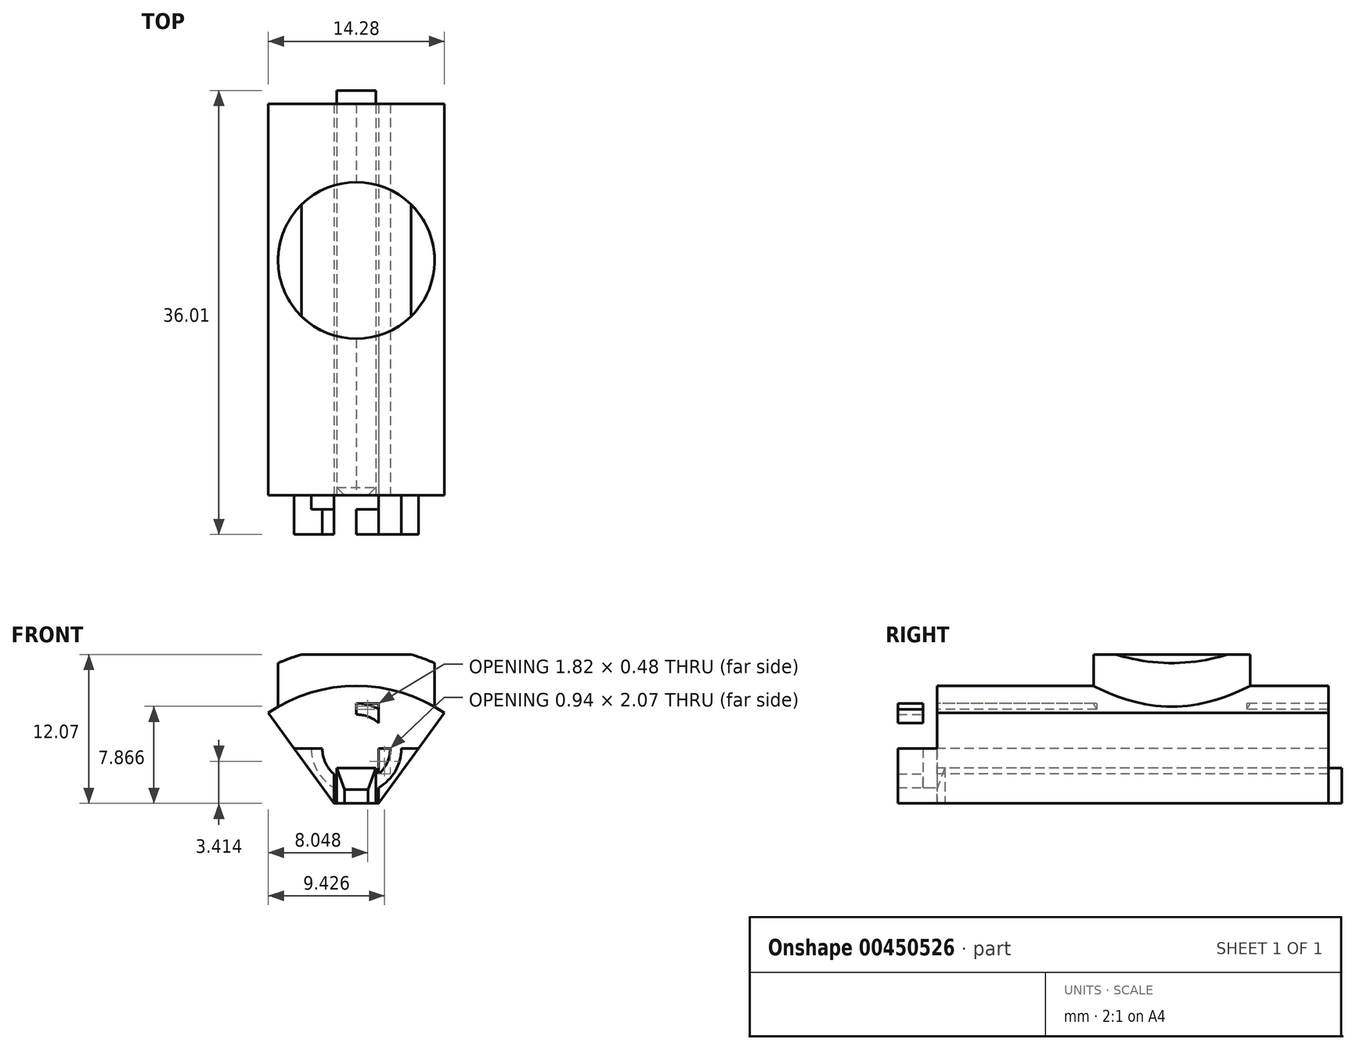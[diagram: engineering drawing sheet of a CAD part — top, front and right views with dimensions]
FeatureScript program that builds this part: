
annotation { "Feature Type Name" : "Feature", "Feature Type Description" : "" }
export const myFeature = defineFeature(function(context is Context, id is Id, definition is map)
    precondition{}
    {
        {
            var Q0;
            Q0=qCreatedBy(makeId("Front.planeOp"),FACE);
            var sketch = newSketch(context, id + "F0", { "sketchPlane" : qUnion([Q0])});
            skLineSegment(sketch, "E0", {"start": v(0, 0) * mm, "end": v(-7.46, 10.27) * mm});
            skLineSegment(sketch, "E1", {"start": v(0, 0) * mm, "end": v(7.46, 10.27) * mm});
            skArc(sketch, "E2", {"start": v(7.46, 10.27) * mm, "mid": v(0, 12.7) * mm, "end": v(-7.46, 10.27) * mm});
            skCircle(sketch, "E3", {"center": v(0, 7.62) * mm, "radius": 3.97 * mm});
            skCircle(sketch, "E4", {"center": v(0, 7.62) * mm, "radius": 3.66 * mm});
            skCircle(sketch, "E5", {"center": v(0, 7.62) * mm, "radius": 2.76 * mm});
            skLineSegment(sketch, "E6", {"start": v(3.41, 5.37) * mm, "end": v(7.14, 10.5) * mm});
            skLineSegment(sketch, "E7", {"start": v(3.41, 5.37) * mm, "end": v(0, 0.68) * mm});
            skLineSegment(sketch, "E8", {"start": v(-3.41, 5.37) * mm, "end": v(-7.14, 10.5) * mm});
            skLineSegment(sketch, "E9", {"start": v(-3.41, 5.37) * mm, "end": v(0, 0.68) * mm});
            skLineSegment(sketch, "E10", {"start": v(0, 11.28) * mm, "end": v(5.84, 11.28) * mm});
            skLineSegment(sketch, "E11", {"start": v(0, 11.28) * mm, "end": v(-5.84, 11.28) * mm});
            skPoint(sketch, "E12.orphan", {"position": v(0, 12.7) * mm});
            skArc(sketch, "E13", {"start": v(1.87, 2.57) * mm, "mid": v(0, 3.17) * mm, "end": v(-1.87, 2.57) * mm});
            skArc(sketch, "E14", {"start": v(-5.6, 7.7) * mm, "mid": v(-4.37, 9.58) * mm, "end": v(-4.68, 11.8) * mm});
            skArc(sketch, "E15", {"start": v(4.68, 11.8) * mm, "mid": v(4.37, 9.58) * mm, "end": v(5.6, 7.7) * mm});
            skLineSegment(sketch, "E16", {"start": v(0, 7.62) * mm, "end": v(-5.54, 7.62) * mm});
            skLineSegment(sketch, "E17", {"start": v(0, 7.62) * mm, "end": v(5.54, 7.62) * mm});
            skLineSegment(sketch, "E18", {"start": v(-1.82, 3.17) * mm, "end": v(-1.82, 12.57) * mm});
            skLineSegment(sketch, "E19", {"start": v(1.82, 3.17) * mm, "end": v(1.82, 12.57) * mm});
            skLineSegment(sketch, "E20", {"start": v(0, 6.03) * mm, "end": v(1.82, 6.03) * mm});
            skLineSegment(sketch, "E21", {"start": v(0, 6.03) * mm, "end": v(-1.82, 6.03) * mm});
            skLineSegment(sketch, "E22", {"start": v(0, 12.7) * mm, "end": v(0, 9.53) * mm});
            skLineSegment(sketch, "E23", {"start": v(0, 9.53) * mm, "end": v(-1.82, 9.53) * mm});
            skLineSegment(sketch, "E24", {"start": v(0, 9.53) * mm, "end": v(1.82, 9.53) * mm});
            skLineSegment(sketch, "E25", {"start": v(0, 0) * mm, "end": v(0, 6.03) * mm});
            skLineSegment(sketch, "E26", {"start": v(0, 3.17) * mm, "end": v(0.8, 3.17) * mm});
            skLineSegment(sketch, "E27", {"start": v(0, 3.17) * mm, "end": v(-0.8, 3.17) * mm});
            skLineSegment(sketch, "E28", {"start": v(0.8, 3.17) * mm, "end": v(1.82, 3.17) * mm});
            skLineSegment(sketch, "E29", {"start": v(-0.8, 3.17) * mm, "end": v(-1.82, 3.17) * mm});
            skLineSegment(sketch, "E30", {"start": v(0, 6.03) * mm, "end": v(-1.59, 6.03) * mm});
            skLineSegment(sketch, "E31", {"start": v(0, 6.03) * mm, "end": v(1.59, 6.03) * mm});
            skLineSegment(sketch, "E32", {"start": v(1.59, 6.03) * mm, "end": v(1.59, 3.17) * mm});
            skLineSegment(sketch, "E33", {"start": v(-1.59, 6.03) * mm, "end": v(-1.59, 3.17) * mm});
            skSolve(sketch);
        }
        {
            var Q0;
            {var subQ0=sQuery(id+"F0.wireOp",EDGE,"E14");var subQ1=sQuery(id+"F0.wireOp",EDGE,"E2");var subQ2=makeQuery(id+"F0.imprint","INTERSECT",VERTEX,{"derivedFrom":[subQ1,subQ0]});Q0=makeQuery(id+"F0.imprint","IMPRINT",FACE,{"disambiguationData":[TD([[makeQuery(id+"F0.imprint","IMPRINT",EDGE,{"disambiguationData":[TD([[subQ2,1.0]])],"derivedFrom":subQ1}),1.0]])]});}
            var Q1;
            {var subQ5=sQuery(id+"F0.wireOp",EDGE,"E16");var subQ9=sQuery(id+"F0.wireOp",EDGE,"E3");var subQ11=makeQuery(id+"F0.imprint","INTERSECT",VERTEX,{"derivedFrom":[subQ9,subQ5]});Q1=makeQuery(id+"F0.imprint","IMPRINT",FACE,{"disambiguationData":[TD([[makeQuery(id+"F0.imprint","IMPRINT",EDGE,{"disambiguationData":[TD([[subQ11,1.0]])],"derivedFrom":subQ9}),-1.0]])]});}
            var Q2;
            {var subQ0=sQuery(id+"F0.wireOp",EDGE,"E15");var subQ1=sQuery(id+"F0.wireOp",EDGE,"E2");var subQ2=makeQuery(id+"F0.imprint","INTERSECT",VERTEX,{"derivedFrom":[subQ1,subQ0]});Q2=makeQuery(id+"F0.imprint","IMPRINT",FACE,{"disambiguationData":[TD([[makeQuery(id+"F0.imprint","IMPRINT",EDGE,{"disambiguationData":[TD([[subQ2,-1.0]])],"derivedFrom":subQ1}),1.0]])]});}
            var Q3;
            {var subQ7=sQuery(id+"F0.wireOp",EDGE,"E17");var subQ9=sQuery(id+"F0.wireOp",EDGE,"E3");var subQ10=makeQuery(id+"F0.imprint","INTERSECT",VERTEX,{"derivedFrom":[subQ9,subQ7]});Q3=makeQuery(id+"F0.imprint","IMPRINT",FACE,{"disambiguationData":[TD([[makeQuery(id+"F0.imprint","IMPRINT",EDGE,{"disambiguationData":[TD([[subQ10,-1.0]])],"derivedFrom":subQ9}),-1.0]])]});}
            var Q4;
            {var subQ0=sQuery(id+"F0.wireOp",EDGE,"E17");var subQ1=sQuery(id+"F0.wireOp",EDGE,"E3");var subQ2=makeQuery(id+"F0.imprint","INTERSECT",VERTEX,{"derivedFrom":[subQ1,subQ0]});Q4=makeQuery(id+"F0.imprint","IMPRINT",FACE,{"disambiguationData":[TD([[makeQuery(id+"F0.imprint","IMPRINT",EDGE,{"disambiguationData":[TD([[subQ2,1.0]])],"derivedFrom":subQ1}),-1.0]])]});}
            var Q5;
            {var subQ0=sQuery(id+"F0.wireOp",EDGE,"E16");var subQ1=sQuery(id+"F0.wireOp",EDGE,"E3");var subQ2=makeQuery(id+"F0.imprint","INTERSECT",VERTEX,{"derivedFrom":[subQ1,subQ0]});Q5=makeQuery(id+"F0.imprint","IMPRINT",FACE,{"disambiguationData":[TD([[makeQuery(id+"F0.imprint","IMPRINT",EDGE,{"disambiguationData":[TD([[subQ2,-1.0]])],"derivedFrom":subQ1}),-1.0]])]});}
            var Q6;
            {var subQ0=sQuery(id+"F0.wireOp",EDGE,"E16");var subQ1=sQuery(id+"F0.wireOp",EDGE,"E3");var subQ2=makeQuery(id+"F0.imprint","INTERSECT",VERTEX,{"derivedFrom":[subQ1,subQ0]});Q6=makeQuery(id+"F0.imprint","IMPRINT",FACE,{"disambiguationData":[TD([[makeQuery(id+"F0.imprint","IMPRINT",EDGE,{"disambiguationData":[TD([[subQ2,-1.0]])],"derivedFrom":subQ1}),1.0]])]});}
            var Q7;
            {var subQ0=sQuery(id+"F0.wireOp",EDGE,"E16");var subQ1=sQuery(id+"F0.wireOp",EDGE,"E3");var subQ2=makeQuery(id+"F0.imprint","INTERSECT",VERTEX,{"derivedFrom":[subQ1,subQ0]});Q7=makeQuery(id+"F0.imprint","IMPRINT",FACE,{"disambiguationData":[TD([[makeQuery(id+"F0.imprint","IMPRINT",EDGE,{"disambiguationData":[TD([[subQ2,1.0]])],"derivedFrom":subQ1}),1.0]])]});}
            var Q8;
            {var subQ0=sQuery(id+"F0.wireOp",EDGE,"E18");var subQ1=sQuery(id+"F0.wireOp",EDGE,"E4");var subQ2=makeQuery(id+"F0.imprint","INTERSECT",VERTEX,{"disambiguationData":[OD(0.0)],"derivedFrom":[subQ1,subQ0]});Q8=makeQuery(id+"F0.imprint","IMPRINT",FACE,{"disambiguationData":[TD([[makeQuery(id+"F0.imprint","IMPRINT",EDGE,{"disambiguationData":[TD([[subQ2,-1.0]])],"derivedFrom":subQ1}),1.0]])]});}
            var Q9;
            {var subQ0=sQuery(id+"F0.wireOp",EDGE,"E17");var subQ1=sQuery(id+"F0.wireOp",EDGE,"E4");var subQ2=makeQuery(id+"F0.imprint","INTERSECT",VERTEX,{"derivedFrom":[subQ1,subQ0]});Q9=makeQuery(id+"F0.imprint","IMPRINT",FACE,{"disambiguationData":[TD([[makeQuery(id+"F0.imprint","IMPRINT",EDGE,{"disambiguationData":[TD([[subQ2,-1.0]])],"derivedFrom":subQ1}),1.0]])]});}
            var Q10;
            {var subQ0=sQuery(id+"F0.wireOp",EDGE,"E19");var subQ1=sQuery(id+"F0.wireOp",EDGE,"E4");var subQ2=makeQuery(id+"F0.imprint","INTERSECT",VERTEX,{"disambiguationData":[OD(0.0)],"derivedFrom":[subQ1,subQ0]});Q10=makeQuery(id+"F0.imprint","IMPRINT",FACE,{"disambiguationData":[TD([[makeQuery(id+"F0.imprint","IMPRINT",EDGE,{"disambiguationData":[TD([[subQ2,-1.0]])],"derivedFrom":subQ1}),1.0]])]});}
            var Q11;
            {var subQ0=sQuery(id+"F0.wireOp",EDGE,"E16");var subQ1=sQuery(id+"F0.wireOp",EDGE,"E4");var subQ2=makeQuery(id+"F0.imprint","INTERSECT",VERTEX,{"derivedFrom":[subQ1,subQ0]});Q11=makeQuery(id+"F0.imprint","IMPRINT",FACE,{"disambiguationData":[TD([[makeQuery(id+"F0.imprint","IMPRINT",EDGE,{"disambiguationData":[TD([[subQ2,-1.0]])],"derivedFrom":subQ1}),1.0]])]});}
            var Q12;
            {var subQ0=sQuery(id+"F0.wireOp",EDGE,"E17");var subQ1=sQuery(id+"F0.wireOp",EDGE,"E3");var subQ2=makeQuery(id+"F0.imprint","INTERSECT",VERTEX,{"derivedFrom":[subQ1,subQ0]});Q12=makeQuery(id+"F0.imprint","IMPRINT",FACE,{"disambiguationData":[TD([[makeQuery(id+"F0.imprint","IMPRINT",EDGE,{"disambiguationData":[TD([[subQ2,-1.0]])],"derivedFrom":subQ1}),1.0]])]});}
            var Q13;
            {var subQ0=sQuery(id+"F0.wireOp",EDGE,"E17");var subQ1=sQuery(id+"F0.wireOp",EDGE,"E3");var subQ2=makeQuery(id+"F0.imprint","INTERSECT",VERTEX,{"derivedFrom":[subQ1,subQ0]});Q13=makeQuery(id+"F0.imprint","IMPRINT",FACE,{"disambiguationData":[TD([[makeQuery(id+"F0.imprint","IMPRINT",EDGE,{"disambiguationData":[TD([[subQ2,1.0]])],"derivedFrom":subQ1}),1.0]])]});}
            var Q14;
            {var subQ0=sQuery(id+"F0.wireOp",EDGE,"E18");var subQ1=sQuery(id+"F0.wireOp",EDGE,"E5");var subQ2=makeQuery(id+"F0.imprint","INTERSECT",VERTEX,{"disambiguationData":[OD(0.0)],"derivedFrom":[subQ1,subQ0]});Q14=makeQuery(id+"F0.imprint","IMPRINT",FACE,{"disambiguationData":[TD([[makeQuery(id+"F0.imprint","IMPRINT",EDGE,{"disambiguationData":[TD([[subQ2,-1.0]])],"derivedFrom":subQ1}),1.0]])]});}
            var Q15;
            {var subQ0=sQuery(id+"F0.wireOp",EDGE,"E17");var subQ1=sQuery(id+"F0.wireOp",EDGE,"E5");var subQ2=makeQuery(id+"F0.imprint","INTERSECT",VERTEX,{"derivedFrom":[subQ1,subQ0]});Q15=makeQuery(id+"F0.imprint","IMPRINT",FACE,{"disambiguationData":[TD([[makeQuery(id+"F0.imprint","IMPRINT",EDGE,{"disambiguationData":[TD([[subQ2,-1.0]])],"derivedFrom":subQ1}),1.0]])]});}
            var Q16;
            {var subQ0=sQuery(id+"F0.wireOp",EDGE,"E19");var subQ1=sQuery(id+"F0.wireOp",EDGE,"E5");var subQ2=makeQuery(id+"F0.imprint","INTERSECT",VERTEX,{"disambiguationData":[OD(0.0)],"derivedFrom":[subQ1,subQ0]});Q16=makeQuery(id+"F0.imprint","IMPRINT",FACE,{"disambiguationData":[TD([[makeQuery(id+"F0.imprint","IMPRINT",EDGE,{"disambiguationData":[TD([[subQ2,-1.0]])],"derivedFrom":subQ1}),1.0]])]});}
            var Q17;
            {var subQ0=sQuery(id+"F0.wireOp",EDGE,"E16");var subQ1=sQuery(id+"F0.wireOp",EDGE,"E5");var subQ2=makeQuery(id+"F0.imprint","INTERSECT",VERTEX,{"derivedFrom":[subQ1,subQ0]});Q17=makeQuery(id+"F0.imprint","IMPRINT",FACE,{"disambiguationData":[TD([[makeQuery(id+"F0.imprint","IMPRINT",EDGE,{"disambiguationData":[TD([[subQ2,-1.0]])],"derivedFrom":subQ1}),1.0]])]});}
            var Q18;
            {var subQ1=sQuery(id+"F0.wireOp",EDGE,"E17");var subQ6=sQuery(id+"F0.wireOp",EDGE,"E16");var subQ11=makeQuery(id+"F0.imprint","INTERSECT",VERTEX,{"derivedFrom":[subQ6,subQ1]});Q18=makeQuery(id+"F0.imprint","IMPRINT",FACE,{"disambiguationData":[TD([[makeQuery(id+"F0.imprint","IMPRINT",EDGE,{"disambiguationData":[TD([[subQ11,-1.0]])],"derivedFrom":subQ6}),1.0]])]});}
            var Q19;
            {var subQ7=sQuery(id+"F0.wireOp",EDGE,"E23");Q19=makeQuery(id+"F0.imprint","IMPRINT",FACE,{"disambiguationData":[TD([[makeQuery(id+"F0.imprint","IMPRINT",EDGE,{"derivedFrom":subQ7}),1.0]])]});}
            var Q20;
            {var subQ0=sQuery(id+"F0.wireOp",EDGE,"E11");var subQ1=sQuery(id+"F0.wireOp",EDGE,"E2");var subQ2=makeQuery(id+"F0.imprint","INTERSECT",VERTEX,{"derivedFrom":[subQ1,subQ0]});Q20=makeQuery(id+"F0.imprint","IMPRINT",FACE,{"disambiguationData":[TD([[makeQuery(id+"F0.imprint","IMPRINT",EDGE,{"disambiguationData":[TD([[subQ2,-1.0]])],"derivedFrom":subQ1}),1.0]])]});}
            var Q21;
            {var subQ0=sQuery(id+"F0.wireOp",EDGE,"E14");var subQ1=sQuery(id+"F0.wireOp",EDGE,"E2");var subQ2=makeQuery(id+"F0.imprint","INTERSECT",VERTEX,{"derivedFrom":[subQ1,subQ0]});Q21=makeQuery(id+"F0.imprint","IMPRINT",FACE,{"disambiguationData":[TD([[makeQuery(id+"F0.imprint","IMPRINT",EDGE,{"disambiguationData":[TD([[subQ2,-1.0]])],"derivedFrom":subQ1}),1.0]])]});}
            var Q22;
            {var subQ0=sQuery(id+"F0.wireOp",EDGE,"E15");var subQ1=sQuery(id+"F0.wireOp",EDGE,"E2");var subQ2=makeQuery(id+"F0.imprint","INTERSECT",VERTEX,{"derivedFrom":[subQ1,subQ0]});Q22=makeQuery(id+"F0.imprint","IMPRINT",FACE,{"disambiguationData":[TD([[makeQuery(id+"F0.imprint","IMPRINT",EDGE,{"disambiguationData":[TD([[subQ2,1.0]])],"derivedFrom":subQ1}),1.0]])]});}
            var Q23;
            {var subQ0=sQuery(id+"F0.wireOp",EDGE,"E6");var subQ1=sQuery(id+"F0.wireOp",EDGE,"E2");var subQ2=makeQuery(id+"F0.imprint","INTERSECT",VERTEX,{"derivedFrom":[subQ1,subQ0]});Q23=makeQuery(id+"F0.imprint","IMPRINT",FACE,{"disambiguationData":[TD([[makeQuery(id+"F0.imprint","IMPRINT",EDGE,{"disambiguationData":[TD([[subQ2,-1.0]])],"derivedFrom":subQ1}),1.0]])]});}
            var Q24;
            {var subQ5=sQuery(id+"F0.wireOp",EDGE,"E23");Q24=makeQuery(id+"F0.imprint","IMPRINT",FACE,{"disambiguationData":[TD([[makeQuery(id+"F0.imprint","IMPRINT",EDGE,{"derivedFrom":subQ5}),-1.0]])]});}
            var Q25;
            {var subQ5=sQuery(id+"F0.wireOp",EDGE,"E24");Q25=makeQuery(id+"F0.imprint","IMPRINT",FACE,{"disambiguationData":[TD([[makeQuery(id+"F0.imprint","IMPRINT",EDGE,{"derivedFrom":subQ5}),1.0]])]});}
            var Q26;
            {var subQ3=sQuery(id+"F0.wireOp",EDGE,"E19");var subQ5=sQuery(id+"F0.wireOp",EDGE,"E5");var subQ6=makeQuery(id+"F0.imprint","INTERSECT",VERTEX,{"disambiguationData":[OD(1.0)],"derivedFrom":[subQ5,subQ3]});Q26=makeQuery(id+"F0.imprint","IMPRINT",FACE,{"disambiguationData":[TD([[makeQuery(id+"F0.imprint","IMPRINT",EDGE,{"disambiguationData":[TD([[subQ6,-1.0]])],"derivedFrom":subQ5}),-1.0]])]});}
            var Q27;
            {var subQ0=sQuery(id+"F0.wireOp",EDGE,"E22");var subQ5=sQuery(id+"F0.wireOp",EDGE,"E5");var subQ6=makeQuery(id+"F0.imprint","INTERSECT",VERTEX,{"derivedFrom":[subQ5,subQ0]});Q27=makeQuery(id+"F0.imprint","IMPRINT",FACE,{"disambiguationData":[TD([[makeQuery(id+"F0.imprint","IMPRINT",EDGE,{"disambiguationData":[TD([[subQ6,-1.0]])],"derivedFrom":subQ5}),-1.0]])]});}
            var Q28;
            {var subQ0=sQuery(id+"F0.wireOp",EDGE,"E11");var subQ1=sQuery(id+"F0.wireOp",EDGE,"E3");var subQ2=makeQuery(id+"F0.imprint","INTERSECT",VERTEX,{"derivedFrom":[subQ1,subQ0]});Q28=makeQuery(id+"F0.imprint","IMPRINT",FACE,{"disambiguationData":[TD([[makeQuery(id+"F0.imprint","IMPRINT",EDGE,{"disambiguationData":[TD([[subQ2,-1.0]])],"derivedFrom":subQ1}),1.0]])]});}
            var Q29;
            {var subQ3=sQuery(id+"F0.wireOp",EDGE,"E2");var subQ7=sQuery(id+"F0.wireOp",EDGE,"E22");var subQ9=makeQuery(id+"F0.imprint","INTERSECT",VERTEX,{"derivedFrom":[subQ3,subQ7]});Q29=makeQuery(id+"F0.imprint","IMPRINT",FACE,{"disambiguationData":[TD([[makeQuery(id+"F0.imprint","IMPRINT",EDGE,{"disambiguationData":[TD([[subQ9,-1.0]])],"derivedFrom":subQ3}),1.0]])]});}
            var Q30;
            {var subQ3=sQuery(id+"F0.wireOp",EDGE,"E2");var subQ7=sQuery(id+"F0.wireOp",EDGE,"E22");var subQ9=makeQuery(id+"F0.imprint","INTERSECT",VERTEX,{"derivedFrom":[subQ3,subQ7]});Q30=makeQuery(id+"F0.imprint","IMPRINT",FACE,{"disambiguationData":[TD([[makeQuery(id+"F0.imprint","IMPRINT",EDGE,{"disambiguationData":[TD([[subQ9,1.0]])],"derivedFrom":subQ3}),1.0]])]});}
            var Q31;
            {var subQ0=sQuery(id+"F0.wireOp",EDGE,"E10");var subQ1=sQuery(id+"F0.wireOp",EDGE,"E3");var subQ2=makeQuery(id+"F0.imprint","INTERSECT",VERTEX,{"derivedFrom":[subQ1,subQ0]});Q31=makeQuery(id+"F0.imprint","IMPRINT",FACE,{"disambiguationData":[TD([[makeQuery(id+"F0.imprint","IMPRINT",EDGE,{"disambiguationData":[TD([[subQ2,-1.0]])],"derivedFrom":subQ1}),1.0]])]});}
            var Q32;
            {var subQ0=sQuery(id+"F0.wireOp",EDGE,"E22");var subQ1=sQuery(id+"F0.wireOp",EDGE,"E3");var subQ2=makeQuery(id+"F0.imprint","INTERSECT",VERTEX,{"derivedFrom":[subQ1,subQ0]});Q32=makeQuery(id+"F0.imprint","IMPRINT",FACE,{"disambiguationData":[TD([[makeQuery(id+"F0.imprint","IMPRINT",EDGE,{"disambiguationData":[TD([[subQ2,-1.0]])],"derivedFrom":subQ1}),1.0]])]});}
            var Q33;
            {var subQ0=sQuery(id+"F0.wireOp",EDGE,"E19");var subQ1=sQuery(id+"F0.wireOp",EDGE,"E3");var subQ2=makeQuery(id+"F0.imprint","INTERSECT",VERTEX,{"disambiguationData":[OD(1.0)],"derivedFrom":[subQ1,subQ0]});Q33=makeQuery(id+"F0.imprint","IMPRINT",FACE,{"disambiguationData":[TD([[makeQuery(id+"F0.imprint","IMPRINT",EDGE,{"disambiguationData":[TD([[subQ2,-1.0]])],"derivedFrom":subQ1}),1.0]])]});}
            var Q34;
            {var subQ0=sQuery(id+"F0.wireOp",EDGE,"E11");var subQ1=sQuery(id+"F0.wireOp",EDGE,"E3");var subQ2=makeQuery(id+"F0.imprint","INTERSECT",VERTEX,{"derivedFrom":[subQ1,subQ0]});Q34=makeQuery(id+"F0.imprint","IMPRINT",FACE,{"disambiguationData":[TD([[makeQuery(id+"F0.imprint","IMPRINT",EDGE,{"disambiguationData":[TD([[subQ2,-1.0]])],"derivedFrom":subQ1}),-1.0]])]});}
            var Q35;
            {var subQ0=sQuery(id+"F0.wireOp",EDGE,"E19");var subQ1=sQuery(id+"F0.wireOp",EDGE,"E3");var subQ2=makeQuery(id+"F0.imprint","INTERSECT",VERTEX,{"disambiguationData":[OD(1.0)],"derivedFrom":[subQ1,subQ0]});Q35=makeQuery(id+"F0.imprint","IMPRINT",FACE,{"disambiguationData":[TD([[makeQuery(id+"F0.imprint","IMPRINT",EDGE,{"disambiguationData":[TD([[subQ2,-1.0]])],"derivedFrom":subQ1}),-1.0]])]});}
            var Q36;
            {var subQ0=sQuery(id+"F0.wireOp",EDGE,"E33");var subQ1=sQuery(id+"F0.wireOp",EDGE,"E5");var subQ2=makeQuery(id+"F0.imprint","INTERSECT",VERTEX,{"derivedFrom":[subQ1,subQ0]});Q36=makeQuery(id+"F0.imprint","IMPRINT",FACE,{"disambiguationData":[TD([[makeQuery(id+"F0.imprint","IMPRINT",EDGE,{"disambiguationData":[TD([[subQ2,1.0]])],"derivedFrom":subQ1}),1.0]])]});}
            var Q37;
            {var subQ0=sQuery(id+"F0.wireOp",EDGE,"E18");var subQ1=sQuery(id+"F0.wireOp",EDGE,"E4");var subQ2=makeQuery(id+"F0.imprint","INTERSECT",VERTEX,{"disambiguationData":[OD(1.0)],"derivedFrom":[subQ1,subQ0]});Q37=makeQuery(id+"F0.imprint","IMPRINT",FACE,{"disambiguationData":[TD([[makeQuery(id+"F0.imprint","IMPRINT",EDGE,{"disambiguationData":[TD([[subQ2,-1.0]])],"derivedFrom":subQ1}),1.0]])]});}
            var Q38;
            {var subQ0=sQuery(id+"F0.wireOp",EDGE,"E33");var subQ1=sQuery(id+"F0.wireOp",EDGE,"E3");var subQ2=makeQuery(id+"F0.imprint","INTERSECT",VERTEX,{"derivedFrom":[subQ1,subQ0]});Q38=makeQuery(id+"F0.imprint","IMPRINT",FACE,{"disambiguationData":[TD([[makeQuery(id+"F0.imprint","IMPRINT",EDGE,{"disambiguationData":[TD([[subQ2,1.0]])],"derivedFrom":subQ1}),1.0]])]});}
            var Q39;
            {var subQ0=sQuery(id+"F0.wireOp",EDGE,"E33");var subQ1=sQuery(id+"F0.wireOp",EDGE,"E3");var subQ2=makeQuery(id+"F0.imprint","INTERSECT",VERTEX,{"derivedFrom":[subQ1,subQ0]});Q39=makeQuery(id+"F0.imprint","IMPRINT",FACE,{"disambiguationData":[TD([[makeQuery(id+"F0.imprint","IMPRINT",EDGE,{"disambiguationData":[TD([[subQ2,1.0]])],"derivedFrom":subQ1}),-1.0]])]});}
            var Q40;
            {var subQ0=sQuery(id+"F0.wireOp",EDGE,"E32");var subQ1=sQuery(id+"F0.wireOp",EDGE,"E5");var subQ2=makeQuery(id+"F0.imprint","INTERSECT",VERTEX,{"derivedFrom":[subQ1,subQ0]});Q40=makeQuery(id+"F0.imprint","IMPRINT",FACE,{"disambiguationData":[TD([[makeQuery(id+"F0.imprint","IMPRINT",EDGE,{"disambiguationData":[TD([[subQ2,-1.0]])],"derivedFrom":subQ1}),1.0]])]});}
            var Q41;
            {var subQ0=sQuery(id+"F0.wireOp",EDGE,"E32");var subQ1=sQuery(id+"F0.wireOp",EDGE,"E4");var subQ2=makeQuery(id+"F0.imprint","INTERSECT",VERTEX,{"derivedFrom":[subQ1,subQ0]});Q41=makeQuery(id+"F0.imprint","IMPRINT",FACE,{"disambiguationData":[TD([[makeQuery(id+"F0.imprint","IMPRINT",EDGE,{"disambiguationData":[TD([[subQ2,-1.0]])],"derivedFrom":subQ1}),1.0]])]});}
            var Q42;
            {var subQ0=sQuery(id+"F0.wireOp",EDGE,"E32");var subQ1=sQuery(id+"F0.wireOp",EDGE,"E3");var subQ2=makeQuery(id+"F0.imprint","INTERSECT",VERTEX,{"derivedFrom":[subQ1,subQ0]});Q42=makeQuery(id+"F0.imprint","IMPRINT",FACE,{"disambiguationData":[TD([[makeQuery(id+"F0.imprint","IMPRINT",EDGE,{"disambiguationData":[TD([[subQ2,-1.0]])],"derivedFrom":subQ1}),1.0]])]});}
            var Q43;
            {var subQ0=sQuery(id+"F0.wireOp",EDGE,"E32");var subQ1=sQuery(id+"F0.wireOp",EDGE,"E3");var subQ2=makeQuery(id+"F0.imprint","INTERSECT",VERTEX,{"derivedFrom":[subQ1,subQ0]});Q43=makeQuery(id+"F0.imprint","IMPRINT",FACE,{"disambiguationData":[TD([[makeQuery(id+"F0.imprint","IMPRINT",EDGE,{"disambiguationData":[TD([[subQ2,-1.0]])],"derivedFrom":subQ1}),-1.0]])]});}
            extrude(context, id + "F1", {"entities" : qUnion([Q0, Q1, Q2, Q3, Q4, Q5, Q6, Q7, Q8, Q9, Q10, Q11, Q12, Q13, Q14, Q15, Q16, Q17, Q18, Q19, Q20, Q21, Q22, Q23, Q24, Q25, Q26, Q27, Q28, Q29, Q30, Q31, Q32, Q33, Q34, Q35, Q36, Q37, Q38, Q39, Q40, Q41, Q42, Q43]), "oppositeDirection" : true, "depth" : 31.75 * mm});
        }
        {
            var Q0;
            {var subQ0=sQuery(id+"F0.wireOp",EDGE,"E16");var subQ1=sQuery(id+"F0.wireOp",EDGE,"E3");var subQ2=makeQuery(id+"F0.imprint","INTERSECT",VERTEX,{"derivedFrom":[subQ1,subQ0]});Q0=makeQuery(id+"F0.imprint","IMPRINT",FACE,{"disambiguationData":[TD([[makeQuery(id+"F0.imprint","IMPRINT",EDGE,{"disambiguationData":[TD([[subQ2,-1.0]])],"derivedFrom":subQ1}),-1.0]])]});}
            var Q1;
            {var subQ0=sQuery(id+"F0.wireOp",EDGE,"E16");var subQ1=sQuery(id+"F0.wireOp",EDGE,"E3");var subQ2=makeQuery(id+"F0.imprint","INTERSECT",VERTEX,{"derivedFrom":[subQ1,subQ0]});Q1=makeQuery(id+"F0.imprint","IMPRINT",FACE,{"disambiguationData":[TD([[makeQuery(id+"F0.imprint","IMPRINT",EDGE,{"disambiguationData":[TD([[subQ2,-1.0]])],"derivedFrom":subQ1}),1.0]])]});}
            var Q2;
            {var subQ0=sQuery(id+"F0.wireOp",EDGE,"E16");var subQ1=sQuery(id+"F0.wireOp",EDGE,"E4");var subQ2=makeQuery(id+"F0.imprint","INTERSECT",VERTEX,{"derivedFrom":[subQ1,subQ0]});Q2=makeQuery(id+"F0.imprint","IMPRINT",FACE,{"disambiguationData":[TD([[makeQuery(id+"F0.imprint","IMPRINT",EDGE,{"disambiguationData":[TD([[subQ2,-1.0]])],"derivedFrom":subQ1}),1.0]])]});}
            var Q3;
            {var subQ0=sQuery(id+"F0.wireOp",EDGE,"E19");var subQ1=sQuery(id+"F0.wireOp",EDGE,"E4");var subQ2=makeQuery(id+"F0.imprint","INTERSECT",VERTEX,{"disambiguationData":[OD(0.0)],"derivedFrom":[subQ1,subQ0]});Q3=makeQuery(id+"F0.imprint","IMPRINT",FACE,{"disambiguationData":[TD([[makeQuery(id+"F0.imprint","IMPRINT",EDGE,{"disambiguationData":[TD([[subQ2,-1.0]])],"derivedFrom":subQ1}),1.0]])]});}
            var Q4;
            {var subQ0=sQuery(id+"F0.wireOp",EDGE,"E17");var subQ1=sQuery(id+"F0.wireOp",EDGE,"E3");var subQ2=makeQuery(id+"F0.imprint","INTERSECT",VERTEX,{"derivedFrom":[subQ1,subQ0]});Q4=makeQuery(id+"F0.imprint","IMPRINT",FACE,{"disambiguationData":[TD([[makeQuery(id+"F0.imprint","IMPRINT",EDGE,{"disambiguationData":[TD([[subQ2,1.0]])],"derivedFrom":subQ1}),1.0]])]});}
            var Q5;
            {var subQ0=sQuery(id+"F0.wireOp",EDGE,"E17");var subQ1=sQuery(id+"F0.wireOp",EDGE,"E3");var subQ2=makeQuery(id+"F0.imprint","INTERSECT",VERTEX,{"derivedFrom":[subQ1,subQ0]});Q5=makeQuery(id+"F0.imprint","IMPRINT",FACE,{"disambiguationData":[TD([[makeQuery(id+"F0.imprint","IMPRINT",EDGE,{"disambiguationData":[TD([[subQ2,1.0]])],"derivedFrom":subQ1}),-1.0]])]});}
            extrude(context, id + "F2", {"entities" : qUnion([Q0, Q1, Q2, Q3, Q4, Q5]), "operationType" : NewBodyOperationType.ADD, "depth" : 3.17 * mm});
        }
        {
            var Q0;
            {var subQ0=sQuery(id+"F0.wireOp",EDGE,"E19");var subQ1=sQuery(id+"F0.wireOp",EDGE,"E4");var subQ2=makeQuery(id+"F0.imprint","INTERSECT",VERTEX,{"disambiguationData":[OD(0.0)],"derivedFrom":[subQ1,subQ0]});Q0=makeQuery(id+"F0.imprint","IMPRINT",FACE,{"disambiguationData":[TD([[makeQuery(id+"F0.imprint","IMPRINT",EDGE,{"disambiguationData":[TD([[subQ2,-1.0]])],"derivedFrom":subQ1}),1.0]])]});}
            var Q1;
            {var subQ0=sQuery(id+"F0.wireOp",EDGE,"E16");var subQ1=sQuery(id+"F0.wireOp",EDGE,"E4");var subQ2=makeQuery(id+"F0.imprint","INTERSECT",VERTEX,{"derivedFrom":[subQ1,subQ0]});Q1=makeQuery(id+"F0.imprint","IMPRINT",FACE,{"disambiguationData":[TD([[makeQuery(id+"F0.imprint","IMPRINT",EDGE,{"disambiguationData":[TD([[subQ2,-1.0]])],"derivedFrom":subQ1}),1.0]])]});}
            extrude(context, id + "F3", {"entities" : qUnion([Q0, Q1]), "operationType" : NewBodyOperationType.REMOVE, "depth" : 1.14 * mm});
        }
        {
            var Q0;
            {var subQ0=sQuery(id+"F0.wireOp",EDGE,"E33");var subQ1=sQuery(id+"F0.wireOp",EDGE,"E5");var subQ2=makeQuery(id+"F0.imprint","INTERSECT",VERTEX,{"derivedFrom":[subQ1,subQ0]});Q0=makeQuery(id+"F0.imprint","IMPRINT",FACE,{"disambiguationData":[TD([[makeQuery(id+"F0.imprint","IMPRINT",EDGE,{"disambiguationData":[TD([[subQ2,-1.0]])],"derivedFrom":subQ1}),1.0]])]});}
            var Q1;
            {var subQ0=sQuery(id+"F0.wireOp",EDGE,"E32");var subQ1=sQuery(id+"F0.wireOp",EDGE,"E5");var subQ2=makeQuery(id+"F0.imprint","INTERSECT",VERTEX,{"derivedFrom":[subQ1,subQ0]});Q1=makeQuery(id+"F0.imprint","IMPRINT",FACE,{"disambiguationData":[TD([[makeQuery(id+"F0.imprint","IMPRINT",EDGE,{"disambiguationData":[TD([[subQ2,1.0]])],"derivedFrom":subQ1}),1.0]])]});}
            var Q2;
            {var subQ0=sQuery(id+"F0.wireOp",EDGE,"E25");var subQ1=sQuery(id+"F0.wireOp",EDGE,"E4");var subQ2=makeQuery(id+"F0.imprint","INTERSECT",VERTEX,{"derivedFrom":[subQ1,subQ0]});Q2=makeQuery(id+"F0.imprint","IMPRINT",FACE,{"disambiguationData":[TD([[makeQuery(id+"F0.imprint","IMPRINT",EDGE,{"disambiguationData":[TD([[subQ2,-1.0]])],"derivedFrom":subQ1}),1.0]])]});}
            var Q3;
            {var subQ0=sQuery(id+"F0.wireOp",EDGE,"E25");var subQ1=sQuery(id+"F0.wireOp",EDGE,"E4");var subQ2=makeQuery(id+"F0.imprint","INTERSECT",VERTEX,{"derivedFrom":[subQ1,subQ0]});Q3=makeQuery(id+"F0.imprint","IMPRINT",FACE,{"disambiguationData":[TD([[makeQuery(id+"F0.imprint","IMPRINT",EDGE,{"disambiguationData":[TD([[subQ2,1.0]])],"derivedFrom":subQ1}),1.0]])]});}
            var Q4;
            {var subQ0=sQuery(id+"F0.wireOp",EDGE,"E33");var subQ1=sQuery(id+"F0.wireOp",EDGE,"E3");var subQ2=makeQuery(id+"F0.imprint","INTERSECT",VERTEX,{"derivedFrom":[subQ1,subQ0]});Q4=makeQuery(id+"F0.imprint","IMPRINT",FACE,{"disambiguationData":[TD([[makeQuery(id+"F0.imprint","IMPRINT",EDGE,{"disambiguationData":[TD([[subQ2,-1.0]])],"derivedFrom":subQ1}),1.0]])]});}
            var Q5;
            {var subQ0=sQuery(id+"F0.wireOp",EDGE,"E32");var subQ1=sQuery(id+"F0.wireOp",EDGE,"E3");var subQ2=makeQuery(id+"F0.imprint","INTERSECT",VERTEX,{"derivedFrom":[subQ1,subQ0]});Q5=makeQuery(id+"F0.imprint","IMPRINT",FACE,{"disambiguationData":[TD([[makeQuery(id+"F0.imprint","IMPRINT",EDGE,{"disambiguationData":[TD([[subQ2,1.0]])],"derivedFrom":subQ1}),1.0]])]});}
            var Q6;
            {var subQ1=sQuery(id+"F0.wireOp",EDGE,"E26");Q6=makeQuery(id+"F0.imprint","IMPRINT",FACE,{"disambiguationData":[TD([[makeQuery(id+"F0.imprint","IMPRINT",EDGE,{"derivedFrom":subQ1}),1.0]])]});}
            var Q7;
            {var subQ0=sQuery(id+"F0.wireOp",EDGE,"E27");Q7=makeQuery(id+"F0.imprint","IMPRINT",FACE,{"disambiguationData":[TD([[makeQuery(id+"F0.imprint","IMPRINT",EDGE,{"derivedFrom":subQ0}),-1.0]])]});}
            extrude(context, id + "F4", {"entities" : qUnion([Q0, Q1, Q2, Q3, Q4, Q5, Q6, Q7]), "oppositeDirection" : true, "depth" : 32.84 * mm});
        }
        {
            var Q0;
            Q0=qCreatedBy(makeId("Top.planeOp"),FACE);
            cPlane(context, id + "F5", {"entities" : qUnion([Q0]), "cplaneType" : CPlaneType.OFFSET, "offset" : 10.16 * mm, "width" : 152.4 * mm, "height" : 152.4 * mm});
        }
        {
            var Q0;
            Q0=qCreatedBy(id+"F5.planeOp",FACE);
            var sketch = newSketch(context, id + "F6", { "sketchPlane" : qUnion([Q0])});
            skLineSegment(sketch, "E34", {"start": v(0, 0) * mm, "end": v(0, 19.05) * mm});
            skCircle(sketch, "E35", {"center": v(0, 19.05) * mm, "radius": 6.35 * mm});
            skSolve(sketch);
        }
        {
            var Q0;
            Q0=makeQuery(id+"F6.imprint","IMPRINT",FACE,{"disambiguationData":[TD([[makeQuery(id+"F6.imprint","IMPRINT",EDGE,{"derivedFrom":sQuery(id+"F6.wireOp",EDGE,"E35")}),1.0]])]});
            extrude(context, id + "F7", {"entities" : qUnion([Q0]), "operationType" : NewBodyOperationType.ADD, "depth" : 5.08 * mm});
        }
        {
            var Q0;
            Q0=qCreatedBy(makeId("Front.planeOp"),FACE);
            var sketch = newSketch(context, id + "F8", { "sketchPlane" : qUnion([Q0])});
            skCircle(sketch, "E36", {"center": v(0, 0) * mm, "radius": 15.88 * mm});
            skCircle(sketch, "E37", {"center": v(0, 0) * mm, "radius": 19.05 * mm});
            skSolve(sketch);
        }
        {
            var Q0;
            Q0=makeQuery(id+"F8.imprint","IMPRINT",FACE,{"disambiguationData":[TD([[makeQuery(id+"F8.imprint","IMPRINT",EDGE,{"derivedFrom":sQuery(id+"F8.wireOp",EDGE,"E36")}),-1.0]])]});
            extrude(context, id + "F9", {"entities" : qUnion([Q0]), "operationType" : NewBodyOperationType.REMOVE, "oppositeDirection" : true, "depth" : 50.8 * mm});
        }
        {
            var Q0;
            Q0=qCreatedBy(makeId("Top.planeOp"),FACE);
            var sketch = newSketch(context, id + "F10", { "sketchPlane" : qUnion([Q0])});
            skLineSegment(sketch, "E38", {"start": v(0, 0) * mm, "end": v(0, 50.8) * mm});
            skSolve(sketch);
        }
        {
            var Q0;
            Q0=makeQuery(id+"F4.opExtrude","CAP_EDGE",EDGE,{"disambiguationData":[OSD([sQuery(id+"F0.wireOp",EDGE,"E33")])],"isStart":true});
            var Q1;
            Q1=makeQuery(id+"F4.opExtrude","CAP_EDGE",EDGE,{"disambiguationData":[OSD([sQuery(id+"F0.wireOp",EDGE,"E32")])],"isStart":true});
            chamfer(context, id + "F11", {"entities" : qUnion([Q0, Q1]), "width" : 0.64 * mm});
        }
        {
            var Q0;
            Q0=makeQuery(id+"F4.opExtrude","CAP_EDGE",EDGE,{"disambiguationData":[OSD([sQuery(id+"F0.wireOp",EDGE,"E20"),sQuery(id+"F0.wireOp",EDGE,"E21")])],"isStart":true});
            chamfer(context, id + "F12", {"entities" : qUnion([Q0]), "chamferType" : ChamferType.OFFSET_ANGLE, "width" : 0.64 * mm, "oppositeDirection" : false, "angle" : 70 * degree, "tangentPropagation" : true});
        }
    });
